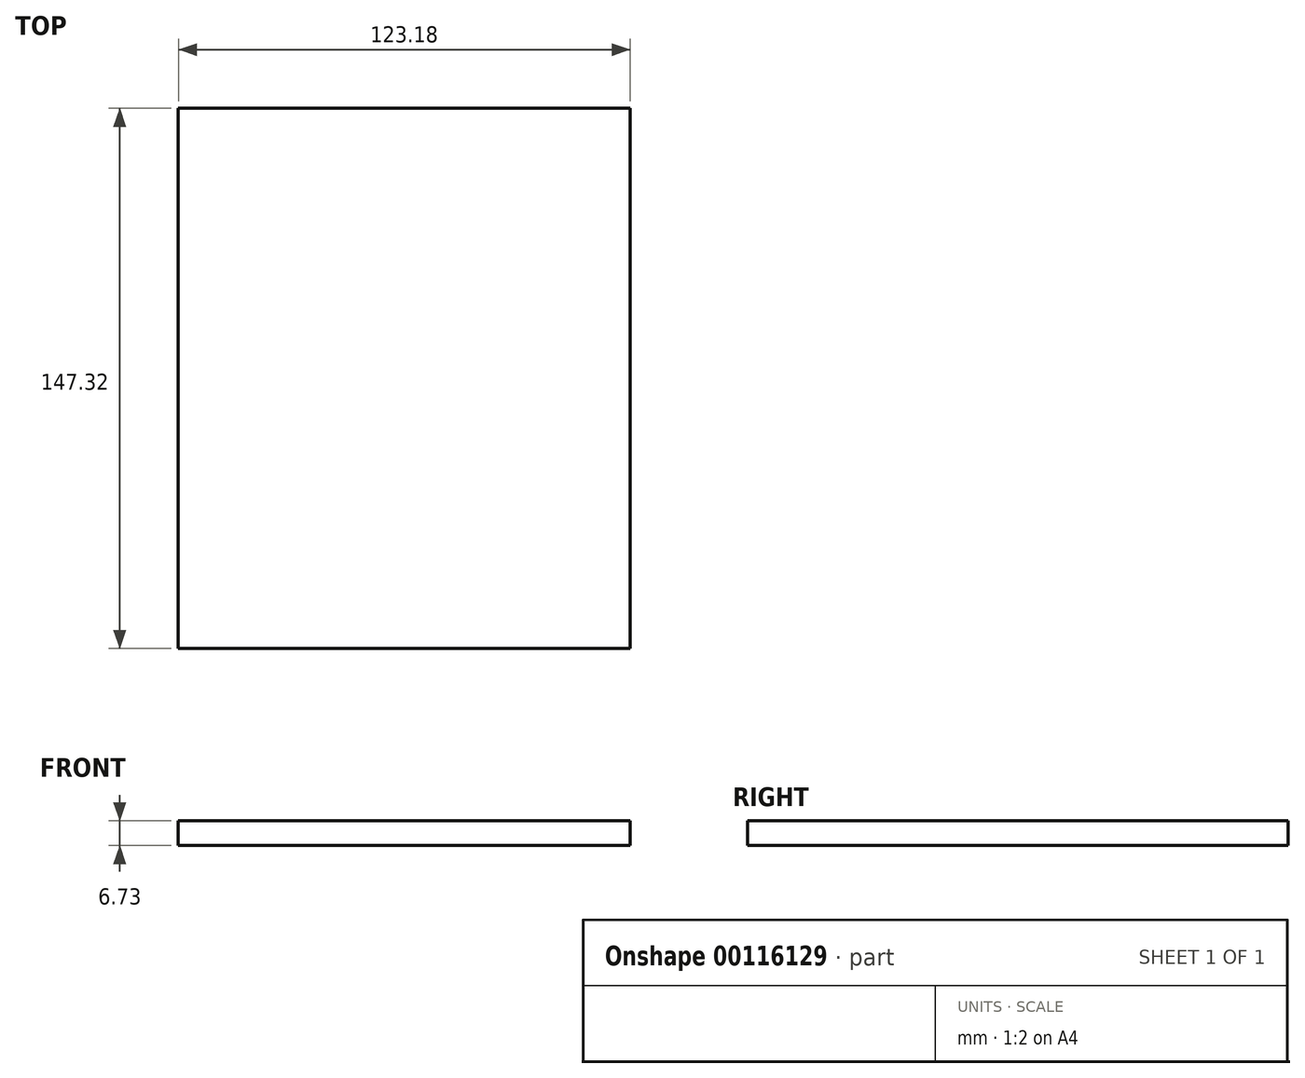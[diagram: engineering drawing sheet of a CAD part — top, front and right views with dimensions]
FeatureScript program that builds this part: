
annotation { "Feature Type Name" : "Feature", "Feature Type Description" : "" }
export const myFeature = defineFeature(function(context is Context, id is Id, definition is map)
    precondition{}
    {
        {
            var Q0;
            Q0=qCreatedBy(makeId("Top.planeOp"),FACE);
            var sketch = newSketch(context, id + "F0", { "sketchPlane" : qUnion([Q0])});
            skLineSegment(sketch, "E0.bottom", {"start": v(61.6, -73.66) * mm, "end": v(-61.6, -73.66) * mm});
            skLineSegment(sketch, "E0.top", {"start": v(61.6, 73.66) * mm, "end": v(-61.6, 73.66) * mm});
            skLineSegment(sketch, "E0.left", {"start": v(61.6, -73.66) * mm, "end": v(61.6, 73.66) * mm});
            skLineSegment(sketch, "E0.right", {"start": v(-61.6, -73.66) * mm, "end": v(-61.6, 73.66) * mm});
            skPoint(sketch, "E0.middle", {"position": v(0, 0) * mm});
            skSolve(sketch);
        }
        {
            var Q0;
            Q0=makeQuery(id+"F0.imprint","IMPRINT",FACE,{"disambiguationData":[TD([[makeQuery(id+"F0.imprint","IMPRINT",EDGE,{"derivedFrom":sQuery(id+"F0.wireOp",EDGE,"E0.bottom")}),-1.0]])]});
            extrude(context, id + "F1", {"entities" : qUnion([Q0]), "depth" : 6.73 * mm});
        }
    });
